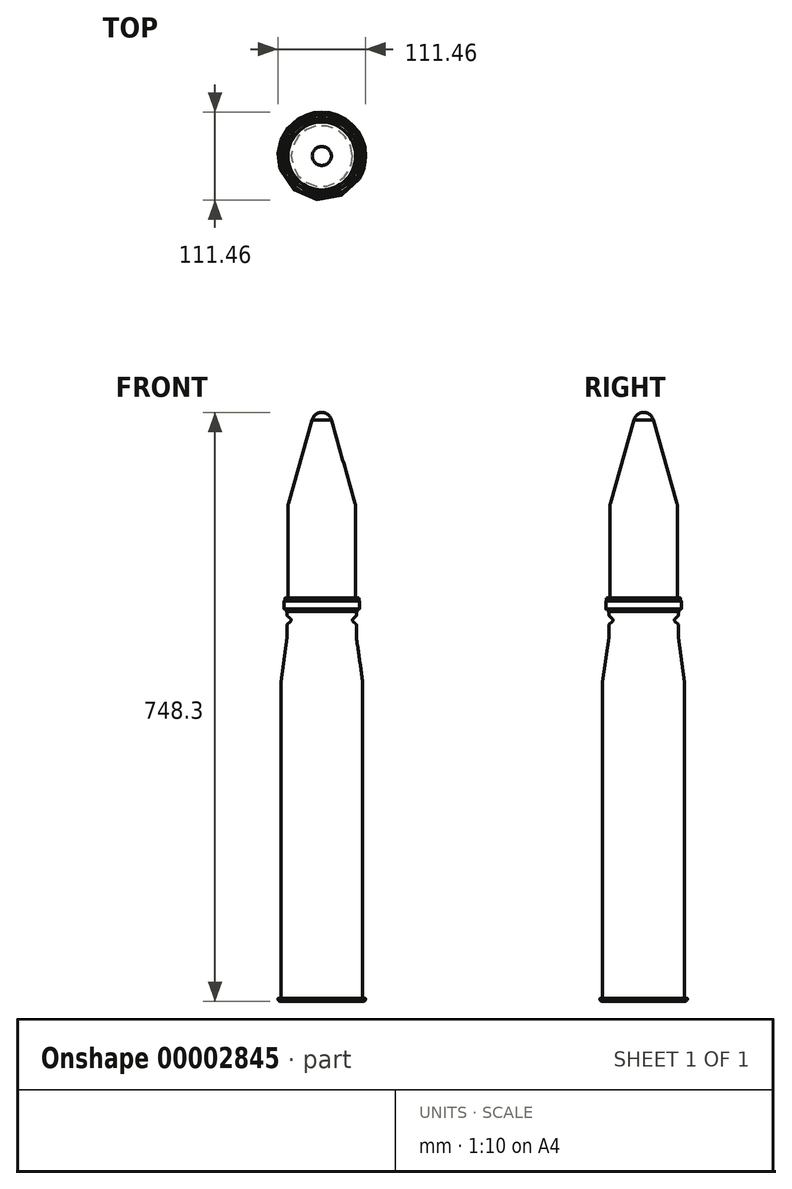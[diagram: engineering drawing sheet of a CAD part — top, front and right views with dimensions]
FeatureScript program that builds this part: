
annotation { "Feature Type Name" : "Feature", "Feature Type Description" : "" }
export const myFeature = defineFeature(function(context is Context, id is Id, definition is map)
    precondition{}
    {
        {
            var Q0;
            Q0=qCreatedBy(makeId("Front.planeOp"),FACE);
            var sketch = newSketch(context, id + "F0", { "sketchPlane" : qUnion([Q0])});
            skLineSegment(sketch, "E0", {"start": v(0, 370.06) * mm, "end": v(0, -378.24) * mm});
            skPoint(sketch, "E1", {"position": v(0, 116.86) * mm});
            skPoint(sketch, "E2", {"position": v(0, 134.26) * mm});
            skLineSegment(sketch, "E3", {"start": v(0, 116.86) * mm, "end": v(-45.59, 116.86) * mm, "construction": true});
            skLineSegment(sketch, "E4", {"start": v(-53, -378.24) * mm, "end": v(0, -378.24) * mm});
            skArc(sketch, "E5", {"start": v(-55.73, -374.91) * mm, "mid": v(-54.85, -376.98) * mm, "end": v(-53, -378.24) * mm});
            skPoint(sketch, "E6.visualSharp", {"position": v(-55.75, -374.24) * mm});
            skArc(sketch, "E6.filletArc", {"start": v(-55.13, -374.24) * mm, "mid": v(-55.58, -374.44) * mm, "end": v(-55.73, -374.91) * mm});
            skLineSegment(sketch, "E7.0.MirrorCS", {"start": v(0, 116.86) * mm, "end": v(45.59, 116.86) * mm, "construction": true});
            skPoint(sketch, "E8.0.start.orphan", {"position": v(0, -374.24) * mm});
            skPoint(sketch, "E9.trimOffspring.end.orphan", {"position": v(-44, 116.86) * mm});
            skPoint(sketch, "E10.visualSharp", {"position": v(-44, 84) * mm});
            skPoint(sketch, "E11.visualSharp", {"position": v(-52, 27.3) * mm});
            skLineSegment(sketch, "E12", {"start": v(-44, 116.86) * mm, "end": v(0, 116.86) * mm});
            skLineSegment(sketch, "E13", {"start": v(-44, 116.86) * mm, "end": v(-45, 116.86) * mm});
            skLineSegment(sketch, "E14", {"start": v(-44, 116.86) * mm, "end": v(-44, 111.98) * mm});
            skPoint(sketch, "E15", {"position": v(-44, 100.43) * mm});
            skLineSegment(sketch, "E16", {"start": v(-44, 100.43) * mm, "end": v(0, 100.43) * mm, "construction": true});
            skLineSegment(sketch, "E17", {"start": v(-45, 116.86) * mm, "end": v(-45, 120.26) * mm});
            skLineSegment(sketch, "E18", {"start": v(-45, 120.26) * mm, "end": v(0, 120.26) * mm});
            skLineSegment(sketch, "E19", {"start": v(-45, 120.26) * mm, "end": v(-48, 120.26) * mm});
            skLineSegment(sketch, "E20", {"start": v(-48, 120.26) * mm, "end": v(-48, 130.26) * mm});
            skLineSegment(sketch, "E21", {"start": v(-48, 130.26) * mm, "end": v(0, 130.26) * mm});
            skLineSegment(sketch, "E22", {"start": v(-47, 130.26) * mm, "end": v(-47, 134.26) * mm});
            skLineSegment(sketch, "E23", {"start": v(-47, 134.26) * mm, "end": v(0, 134.26) * mm});
            skPoint(sketch, "E24", {"position": v(0, 252.16) * mm});
            skLineSegment(sketch, "E25", {"start": v(-44, 84) * mm, "end": v(-44, 100.43) * mm});
            skLineSegment(sketch, "E26", {"start": v(-52, 27.3) * mm, "end": v(-52, -374.24) * mm});
            skLineSegment(sketch, "E27", {"start": v(-55.13, -374.24) * mm, "end": v(-52, -374.24) * mm});
            skLineSegment(sketch, "E28", {"start": v(-44, 84) * mm, "end": v(-52, 27.3) * mm});
            skLineSegment(sketch, "E29", {"start": v(-44, 111.98) * mm, "end": v(0, 111.98) * mm});
            skLineSegment(sketch, "E30", {"start": v(-44, 111.98) * mm, "end": v(-37.9, 106.2) * mm});
            skLineSegment(sketch, "E31", {"start": v(4.07, 106.2) * mm, "end": v(-52.4, 106.2) * mm, "construction": true});
            skLineSegment(sketch, "E32.0.MirrorCS", {"start": v(-44, 100.43) * mm, "end": v(-37.9, 106.2) * mm});
            skLineSegment(sketch, "E33", {"start": v(-43, 252.16) * mm, "end": v(-43, 134.75) * mm});
            skLineSegment(sketch, "E34", {"start": v(-43, 252.16) * mm, "end": v(0, 252.16) * mm});
            skLineSegment(sketch, "E35", {"start": v(-95.4, 370.06) * mm, "end": v(97.65, 370.06) * mm, "construction": true});
            skArc(sketch, "E36", {"start": v(0, 370.06) * mm, "mid": v(-7.7, 367.41) * mm, "end": v(-12.13, 360.6) * mm});
            skLineSegment(sketch, "E37", {"start": v(-12.13, 360.6) * mm, "end": v(-43, 252.16) * mm});
            skLineSegment(sketch, "E38", {"start": v(-42.5, 134.26) * mm, "end": v(-43, 134.75) * mm});
            skPoint(sketch, "E39", {"position": v(-43, 134.75) * mm});
            skPoint(sketch, "E40", {"position": v(-43, 134.26) * mm});
            skSolve(sketch);
        }
        {
            var Q0;
            Q0 = qSketchRegion(id + "F0", true);
            var Q1;
            Q1=sQuery(id+"F0.wireOp",EDGE,"E0");
            revolve(context, id + "F1", {"entities" : qUnion([Q0]), "axis" : qUnion([Q1]), "revolveType" : RevolveType.FULL});
        }
        {
            var Q0;
            Q0=makeQuery(id+"F1.opRevolve","SWEPT_EDGE",EDGE,{"disambiguationData":[OSD([sQuery(id+"F0.wireOp",EDGE,"E30"),sQuery(id+"F0.wireOp",EDGE,"E32.0.MirrorCS")])]});
            fillet(context, id + "F2", {"entities" : qUnion([Q0]), "radius" : 2 * mm, "tangentPropagation" : true, "allowEdgeOverflow" : false});
        }
        {
            var Q0;
            Q0=makeQuery(id+"F1.opRevolve","SWEPT_FACE",FACE,{"disambiguationData":[OSD([sQuery(id+"F0.wireOp",EDGE,"E28")])]});
            fillet(context, id + "F3", {"entities" : qUnion([Q0]), "radius" : 1 * mm, "tangentPropagation" : true, "allowEdgeOverflow" : false});
        }
        {
            var Q0;
            Q0=makeQuery(id+"F1.opRevolve","SWEPT_EDGE",EDGE,{"disambiguationData":[OSD([sQuery(id+"F0.wireOp",EDGE,"E33"),sQuery(id+"F0.wireOp",EDGE,"E34"),sQuery(id+"F0.wireOp",EDGE,"E37")])]});
            fillet(context, id + "F4", {"entities" : qUnion([Q0]), "radius" : 15 * mm, "tangentPropagation" : true, "allowEdgeOverflow" : false});
        }
        {
            var Q0;
            Q0=makeQuery(id+"F1.opRevolve","SWEPT_EDGE",EDGE,{"disambiguationData":[OSD([sQuery(id+"F0.wireOp",EDGE,"E33"),sQuery(id+"F0.wireOp",EDGE,"E38")])]});
            fillet(context, id + "F5", {"entities" : qUnion([Q0]), "radius" : 3 * mm, "tangentPropagation" : true, "allowEdgeOverflow" : false});
        }
        {
            var Q0;
            Q0=makeQuery(id+"F1.opRevolve","SWEPT_FACE",FACE,{"disambiguationData":[OSD([sQuery(id+"F0.wireOp",EDGE,"E17")])]});
            var Q1;
            Q1=makeQuery(id+"F1.opRevolve","SWEPT_FACE",FACE,{"disambiguationData":[OSD([sQuery(id+"F0.wireOp",EDGE,"E14")])]});
            var Q2;
            Q2=makeQuery(id+"F1.opRevolve","SWEPT_EDGE",EDGE,{"disambiguationData":[OSD([sQuery(id+"F0.wireOp",EDGE,"E22"),sQuery(id+"F0.wireOp",EDGE,"E23")])]});
            var Q3;
            Q3=makeQuery(id+"F1.opRevolve","SWEPT_EDGE",EDGE,{"disambiguationData":[OSD([sQuery(id+"F0.wireOp",EDGE,"E20"),sQuery(id+"F0.wireOp",EDGE,"E21")])]});
            var Q4;
            Q4=makeQuery(id+"F1.opRevolve","SWEPT_EDGE",EDGE,{"disambiguationData":[OSD([sQuery(id+"F0.wireOp",EDGE,"E19"),sQuery(id+"F0.wireOp",EDGE,"E20")])]});
            var Q5;
            Q5=makeQuery(id+"F1.opRevolve","SWEPT_EDGE",EDGE,{"disambiguationData":[OSD([sQuery(id+"F0.wireOp",EDGE,"E25"),sQuery(id+"F0.wireOp",EDGE,"E32.0.MirrorCS")])]});
            fillet(context, id + "F6", {"entities" : qUnion([Q0, Q1, Q2, Q3, Q4, Q5]), "radius" : 0.3 * mm, "tangentPropagation" : true, "allowEdgeOverflow" : false});
        }
        {
            var Q0;
            Q0=makeQuery(id+"F5.opFillet","BLEND_EDGE",EDGE,{"blendedFrom":[makeQuery(id+"F1.opRevolve","SWEPT_EDGE",EDGE,{"disambiguationData":[OSD([sQuery(id+"F0.wireOp",EDGE,"E33"),sQuery(id+"F0.wireOp",EDGE,"E38")])]}),makeQuery(id+"F1.opRevolve","SWEPT_FACE",FACE,{"disambiguationData":[OSD([sQuery(id+"F0.wireOp",EDGE,"E23")])]})],"blendedInto":[makeQuery(id+"F1.opRevolve","SWEPT_FACE",FACE,{"disambiguationData":[OSD([sQuery(id+"F0.wireOp",EDGE,"E23")])]})]});
            var Q1;
            Q1=makeQuery(id+"F3.opFillet","BLEND_FACE",FACE,{"disambiguationData":[OSD([sQuery(id+"F0.wireOp",EDGE,"E25"),sQuery(id+"F0.wireOp",EDGE,"E28")])]});
            fillet(context, id + "F7", {"entities" : qUnion([Q0, Q1]), "radius" : 0.1 * mm, "tangentPropagation" : true, "allowEdgeOverflow" : false});
        }
    });
